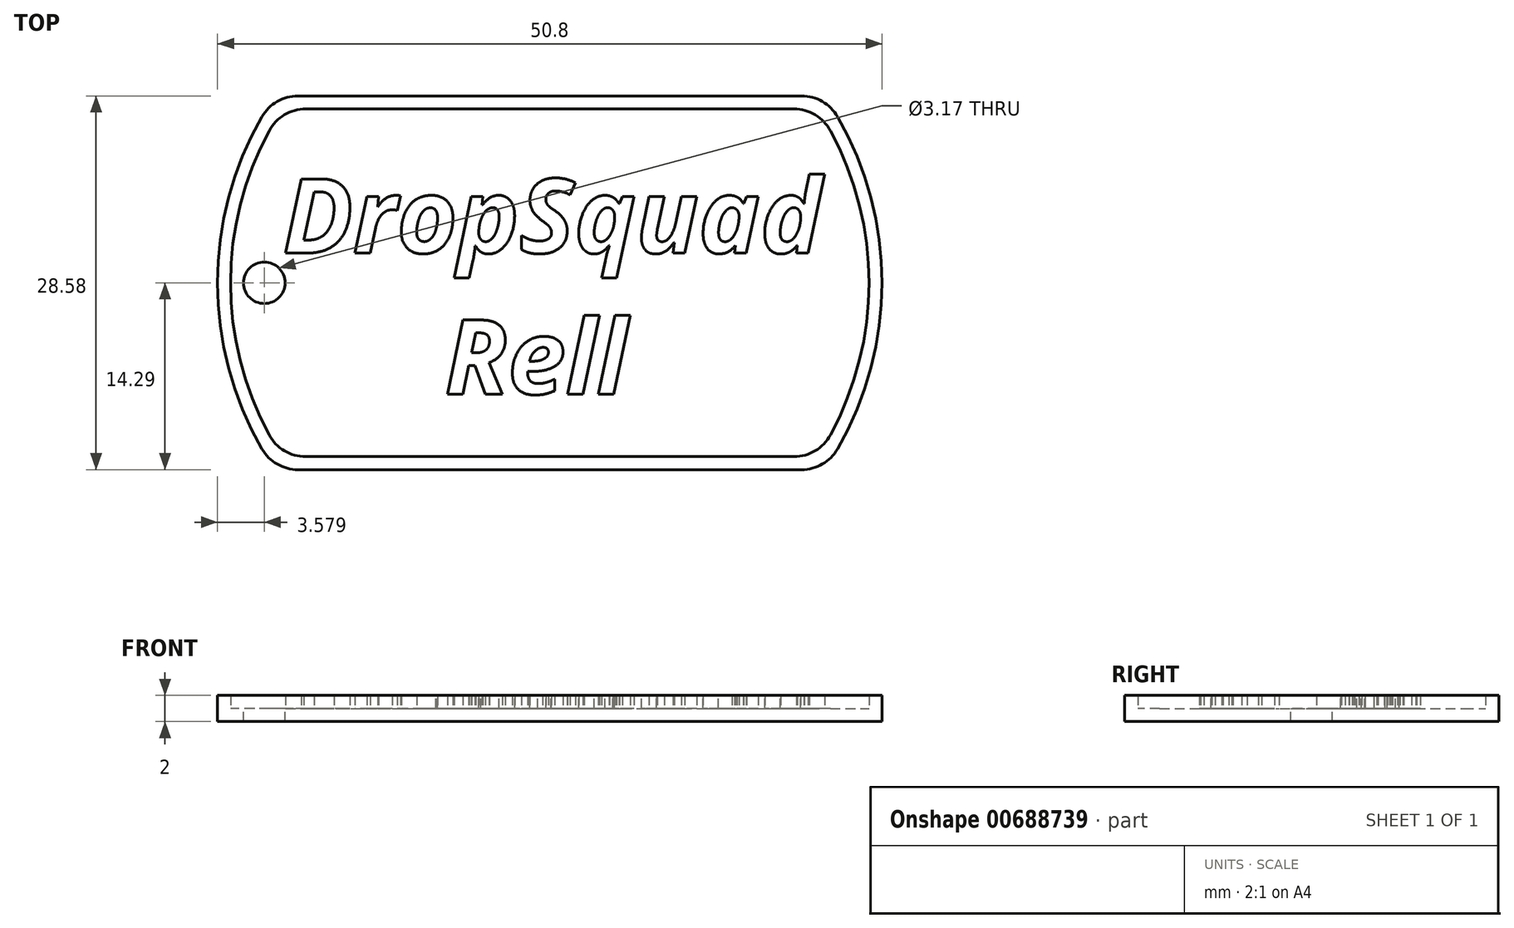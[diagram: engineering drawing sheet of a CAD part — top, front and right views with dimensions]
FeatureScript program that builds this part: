
annotation { "Feature Type Name" : "Feature", "Feature Type Description" : "" }
export const myFeature = defineFeature(function(context is Context, id is Id, definition is map)
    precondition{}
    {
        {
            var Q0;
            Q0=qCreatedBy(makeId("Top.planeOp"),FACE);
            var sketch = newSketch(context, id + "F0", { "sketchPlane" : qUnion([Q0])});
            skArc(sketch, "E0", {"start": v(-22, 12.7) * mm, "mid": v(-25.4, 0) * mm, "end": v(-22, -12.7) * mm});
            skLineSegment(sketch, "E1.top", {"start": v(-19.25, -14.29) * mm, "end": v(19.25, -14.29) * mm});
            skArc(sketch, "E2.trimOffspring", {"start": v(22, -12.7) * mm, "mid": v(25.4, 0) * mm, "end": v(22, 12.7) * mm});
            skLineSegment(sketch, "E3", {"start": v(-19.25, 14.29) * mm, "end": v(19.25, 14.29) * mm});
            skPoint(sketch, "E4.visualSharp", {"position": v(-21, 14.29) * mm});
            skArc(sketch, "E4.filletArc", {"start": v(-19.25, 14.29) * mm, "mid": v(-20.83, 13.86) * mm, "end": v(-22, 12.7) * mm});
            skPoint(sketch, "E5.visualSharp", {"position": v(21, 14.29) * mm});
            skArc(sketch, "E5.filletArc", {"start": v(22, 12.7) * mm, "mid": v(20.83, 13.86) * mm, "end": v(19.25, 14.29) * mm});
            skPoint(sketch, "E6.visualSharp", {"position": v(21, -14.29) * mm});
            skArc(sketch, "E6.filletArc", {"start": v(19.25, -14.29) * mm, "mid": v(20.83, -13.86) * mm, "end": v(22, -12.7) * mm});
            skPoint(sketch, "E7.visualSharp", {"position": v(-21, -14.29) * mm});
            skArc(sketch, "E7.filletArc", {"start": v(-22, -12.7) * mm, "mid": v(-20.83, -13.86) * mm, "end": v(-19.25, -14.29) * mm});
            skSolve(sketch);
        }
        {
            var Q0;
            Q0=makeQuery(id+"F0.imprint","IMPRINT",FACE,{"disambiguationData":[TD([[makeQuery(id+"F0.imprint","IMPRINT",EDGE,{"derivedFrom":sQuery(id+"F0.wireOp",EDGE,"E0")}),1.0]])]});
            extrude(context, id + "F1", {"entities" : qUnion([Q0]), "depth" : 1 * mm, "offsetDistance" : 25.4 * mm});
        }
        {
            var Q0;
            Q0=makeQuery(id+"F1.opExtrude","CAP_FACE",FACE,{"disambiguationData":[OSD([sQuery(id+"F0.wireOp",EDGE,"E0"),sQuery(id+"F0.wireOp",EDGE,"E1.top"),sQuery(id+"F0.wireOp",EDGE,"E2.trimOffspring"),sQuery(id+"F0.wireOp",EDGE,"E3"),sQuery(id+"F0.wireOp",EDGE,"E4.filletArc"),sQuery(id+"F0.wireOp",EDGE,"E5.filletArc"),sQuery(id+"F0.wireOp",EDGE,"E6.filletArc"),sQuery(id+"F0.wireOp",EDGE,"E7.filletArc")])],"isStart":false});
            var sketch = newSketch(context, id + "F2", { "sketchPlane" : qUnion([Q0])});
            skLineSegment(sketch, "E8.0", {"start": v(-18.66, 13.29) * mm, "end": v(18.66, 13.29) * mm});
            skArc(sketch, "E8.1", {"start": v(-21.45, 11.63) * mm, "mid": v(-24.4, 0) * mm, "end": v(-21.45, -11.63) * mm});
            skLineSegment(sketch, "E8.2", {"start": v(-18.66, -13.29) * mm, "end": v(18.66, -13.29) * mm});
            skArc(sketch, "E8.3", {"start": v(21.45, -11.63) * mm, "mid": v(24.4, 0) * mm, "end": v(21.45, 11.63) * mm});
            skPoint(sketch, "E9.visualSharp", {"position": v(-20.46, 13.29) * mm});
            skArc(sketch, "E9.filletArc", {"start": v(-18.66, 13.29) * mm, "mid": v(-20.29, 12.84) * mm, "end": v(-21.45, 11.63) * mm});
            skPoint(sketch, "E10.visualSharp", {"position": v(20.46, 13.29) * mm});
            skArc(sketch, "E10.filletArc", {"start": v(21.45, 11.63) * mm, "mid": v(20.29, 12.84) * mm, "end": v(18.66, 13.29) * mm});
            skPoint(sketch, "E11.visualSharp", {"position": v(20.46, -13.29) * mm});
            skArc(sketch, "E11.filletArc", {"start": v(18.66, -13.29) * mm, "mid": v(20.29, -12.84) * mm, "end": v(21.45, -11.63) * mm});
            skPoint(sketch, "E12.visualSharp", {"position": v(-20.46, -13.29) * mm});
            skArc(sketch, "E12.filletArc", {"start": v(-21.45, -11.63) * mm, "mid": v(-20.29, -12.84) * mm, "end": v(-18.66, -13.29) * mm});
            skLineSegment(sketch, "E13.0", {"start": v(-19.25, 14.29) * mm, "end": v(19.25, 14.29) * mm});
            skArc(sketch, "E13.1", {"start": v(-22, 12.7) * mm, "mid": v(-25.4, 0) * mm, "end": v(-22, -12.7) * mm});
            skLineSegment(sketch, "E13.2", {"start": v(-19.25, -14.29) * mm, "end": v(19.25, -14.29) * mm});
            skArc(sketch, "E13.3", {"start": v(22, -12.7) * mm, "mid": v(25.4, 0) * mm, "end": v(22, 12.7) * mm});
            skPoint(sketch, "E14.visualSharp", {"position": v(-21, -14.29) * mm});
            skArc(sketch, "E14.filletArc", {"start": v(-22, -12.7) * mm, "mid": v(-20.83, -13.86) * mm, "end": v(-19.25, -14.29) * mm});
            skPoint(sketch, "E15.visualSharp", {"position": v(21, -14.29) * mm});
            skArc(sketch, "E15.filletArc", {"start": v(19.25, -14.29) * mm, "mid": v(20.83, -13.86) * mm, "end": v(22, -12.7) * mm});
            skPoint(sketch, "E16.visualSharp", {"position": v(21, 14.29) * mm});
            skArc(sketch, "E16.filletArc", {"start": v(22, 12.7) * mm, "mid": v(20.83, 13.86) * mm, "end": v(19.25, 14.29) * mm});
            skPoint(sketch, "E17.visualSharp", {"position": v(-21, 14.29) * mm});
            skArc(sketch, "E17.filletArc", {"start": v(-19.25, 14.29) * mm, "mid": v(-20.83, 13.86) * mm, "end": v(-22, 12.7) * mm});
            skSolve(sketch);
        }
        {
            var Q0;
            Q0=makeQuery(id+"F2.imprint","IMPRINT",FACE,{"disambiguationData":[TD([[makeQuery(id+"F2.imprint","IMPRINT",EDGE,{"derivedFrom":sQuery(id+"F2.wireOp",EDGE,"E8.0")}),1.0]])]});
            extrude(context, id + "F3", {"entities" : qUnion([Q0]), "operationType" : NewBodyOperationType.ADD, "depth" : 1 * mm, "offsetDistance" : 25.4 * mm});
        }
        {
            var Q0;
            Q0=makeQuery(id+"F1.opExtrude","CAP_FACE",FACE,{"disambiguationData":[OSD([sQuery(id+"F0.wireOp",EDGE,"E0"),sQuery(id+"F0.wireOp",EDGE,"E1.top"),sQuery(id+"F0.wireOp",EDGE,"E2.trimOffspring"),sQuery(id+"F0.wireOp",EDGE,"E3"),sQuery(id+"F0.wireOp",EDGE,"E4.filletArc"),sQuery(id+"F0.wireOp",EDGE,"E5.filletArc"),sQuery(id+"F0.wireOp",EDGE,"E6.filletArc"),sQuery(id+"F0.wireOp",EDGE,"E7.filletArc")])],"isStart":false});
            var sketch = newSketch(context, id + "F4", { "sketchPlane" : qUnion([Q0])});
            skCircle(sketch, "E18", {"center": v(-21.82, 0) * mm, "radius": 1.59 * mm});
            skSolve(sketch);
        }
        {
            var Q0;
            Q0=makeQuery(id+"F4.imprint","IMPRINT",FACE,{"disambiguationData":[TD([[makeQuery(id+"F4.imprint","IMPRINT",EDGE,{"derivedFrom":sQuery(id+"F4.wireOp",EDGE,"E18")}),1.0]])]});
            extrude(context, id + "F5", {"entities" : qUnion([Q0]), "operationType" : NewBodyOperationType.REMOVE, "oppositeDirection" : true, "depth" : 1 * mm, "offsetDistance" : 25.4 * mm});
        }
        {
            var Q0;
            Q0=makeQuery(id+"F1.opExtrude","CAP_FACE",FACE,{"disambiguationData":[OSD([sQuery(id+"F0.wireOp",EDGE,"E0"),sQuery(id+"F0.wireOp",EDGE,"E1.top"),sQuery(id+"F0.wireOp",EDGE,"E2.trimOffspring"),sQuery(id+"F0.wireOp",EDGE,"E3"),sQuery(id+"F0.wireOp",EDGE,"E4.filletArc"),sQuery(id+"F0.wireOp",EDGE,"E5.filletArc"),sQuery(id+"F0.wireOp",EDGE,"E6.filletArc"),sQuery(id+"F0.wireOp",EDGE,"E7.filletArc")])],"isStart":false});
            var sketch = newSketch(context, id + "F6", { "sketchPlane" : qUnion([Q0])});
            skText(sketch, "E19", { "text": "DropSquad\n      Rell ", "fontName": "OpenSans-BoldItalic.ttf"});
            const initialGuessF6  = {"E19": [-0.0204, 0.00228, 1, 0, 0.00571]};
            skSetInitialGuess(sketch, initialGuessF6);
            skSolve(sketch);
        }
        {
            var Q0;
            Q0=makeQuery(id+"F6.imprint","IMPRINT",FACE,{"disambiguationData":[TD([[makeQuery(id+"F6.imprint","IMPRINT",EDGE,{"derivedFrom":sQuery(id+"F6.wireOp",EDGE,"E19.sketch_text.stroke-16")}),-1.0]])]});
            var Q1;
            Q1=makeQuery(id+"F6.imprint","IMPRINT",FACE,{"disambiguationData":[TD([[makeQuery(id+"F6.imprint","IMPRINT",EDGE,{"derivedFrom":sQuery(id+"F6.wireOp",EDGE,"E19.sketch_text.stroke-71")}),-1.0]])]});
            var Q2;
            Q2=makeQuery(id+"F6.imprint","IMPRINT",FACE,{"disambiguationData":[TD([[makeQuery(id+"F6.imprint","IMPRINT",EDGE,{"derivedFrom":sQuery(id+"F6.wireOp",EDGE,"E19.sketch_text.stroke-123")}),-1.0]])]});
            var Q3;
            Q3=makeQuery(id+"F6.imprint","IMPRINT",FACE,{"disambiguationData":[TD([[makeQuery(id+"F6.imprint","IMPRINT",EDGE,{"derivedFrom":sQuery(id+"F6.wireOp",EDGE,"E19.sketch_text.stroke-235")}),-1.0]])]});
            var Q4;
            Q4=makeQuery(id+"F6.imprint","IMPRINT",FACE,{"disambiguationData":[TD([[makeQuery(id+"F6.imprint","IMPRINT",EDGE,{"derivedFrom":sQuery(id+"F6.wireOp",EDGE,"E19.sketch_text.stroke-239")}),-1.0]])]});
            var Q5;
            Q5=makeQuery(id+"F6.imprint","IMPRINT",FACE,{"disambiguationData":[TD([[makeQuery(id+"F6.imprint","IMPRINT",EDGE,{"derivedFrom":sQuery(id+"F6.wireOp",EDGE,"E19.sketch_text.stroke-0")}),-1.0]])]});
            var Q6;
            Q6=makeQuery(id+"F6.imprint","IMPRINT",FACE,{"disambiguationData":[TD([[makeQuery(id+"F6.imprint","IMPRINT",EDGE,{"derivedFrom":sQuery(id+"F6.wireOp",EDGE,"E19.sketch_text.stroke-28")}),-1.0]])]});
            var Q7;
            Q7=makeQuery(id+"F6.imprint","IMPRINT",FACE,{"disambiguationData":[TD([[makeQuery(id+"F6.imprint","IMPRINT",EDGE,{"derivedFrom":sQuery(id+"F6.wireOp",EDGE,"E19.sketch_text.stroke-46")}),-1.0]])]});
            var Q8;
            Q8=makeQuery(id+"F6.imprint","IMPRINT",FACE,{"disambiguationData":[TD([[makeQuery(id+"F6.imprint","IMPRINT",EDGE,{"derivedFrom":sQuery(id+"F6.wireOp",EDGE,"E19.sketch_text.stroke-95")}),-1.0]])]});
            var Q9;
            Q9=makeQuery(id+"F6.imprint","IMPRINT",FACE,{"disambiguationData":[TD([[makeQuery(id+"F6.imprint","IMPRINT",EDGE,{"derivedFrom":sQuery(id+"F6.wireOp",EDGE,"E19.sketch_text.stroke-140")}),-1.0]])]});
            var Q10;
            Q10=makeQuery(id+"F6.imprint","IMPRINT",FACE,{"disambiguationData":[TD([[makeQuery(id+"F6.imprint","IMPRINT",EDGE,{"derivedFrom":sQuery(id+"F6.wireOp",EDGE,"E19.sketch_text.stroke-165")}),-1.0]])]});
            var Q11;
            Q11=makeQuery(id+"F6.imprint","IMPRINT",FACE,{"disambiguationData":[TD([[makeQuery(id+"F6.imprint","IMPRINT",EDGE,{"derivedFrom":sQuery(id+"F6.wireOp",EDGE,"E19.sketch_text.stroke-192")}),-1.0]])]});
            var Q12;
            Q12=makeQuery(id+"F6.imprint","IMPRINT",FACE,{"disambiguationData":[TD([[makeQuery(id+"F6.imprint","IMPRINT",EDGE,{"derivedFrom":sQuery(id+"F6.wireOp",EDGE,"E19.sketch_text.stroke-211")}),-1.0]])]});
            extrude(context, id + "F7", {"entities" : qUnion([Q0, Q1, Q2, Q3, Q4, Q5, Q6, Q7, Q8, Q9, Q10, Q11, Q12]), "operationType" : NewBodyOperationType.ADD, "depth" : 1 * mm, "offsetDistance" : 25.4 * mm});
        }
    });
